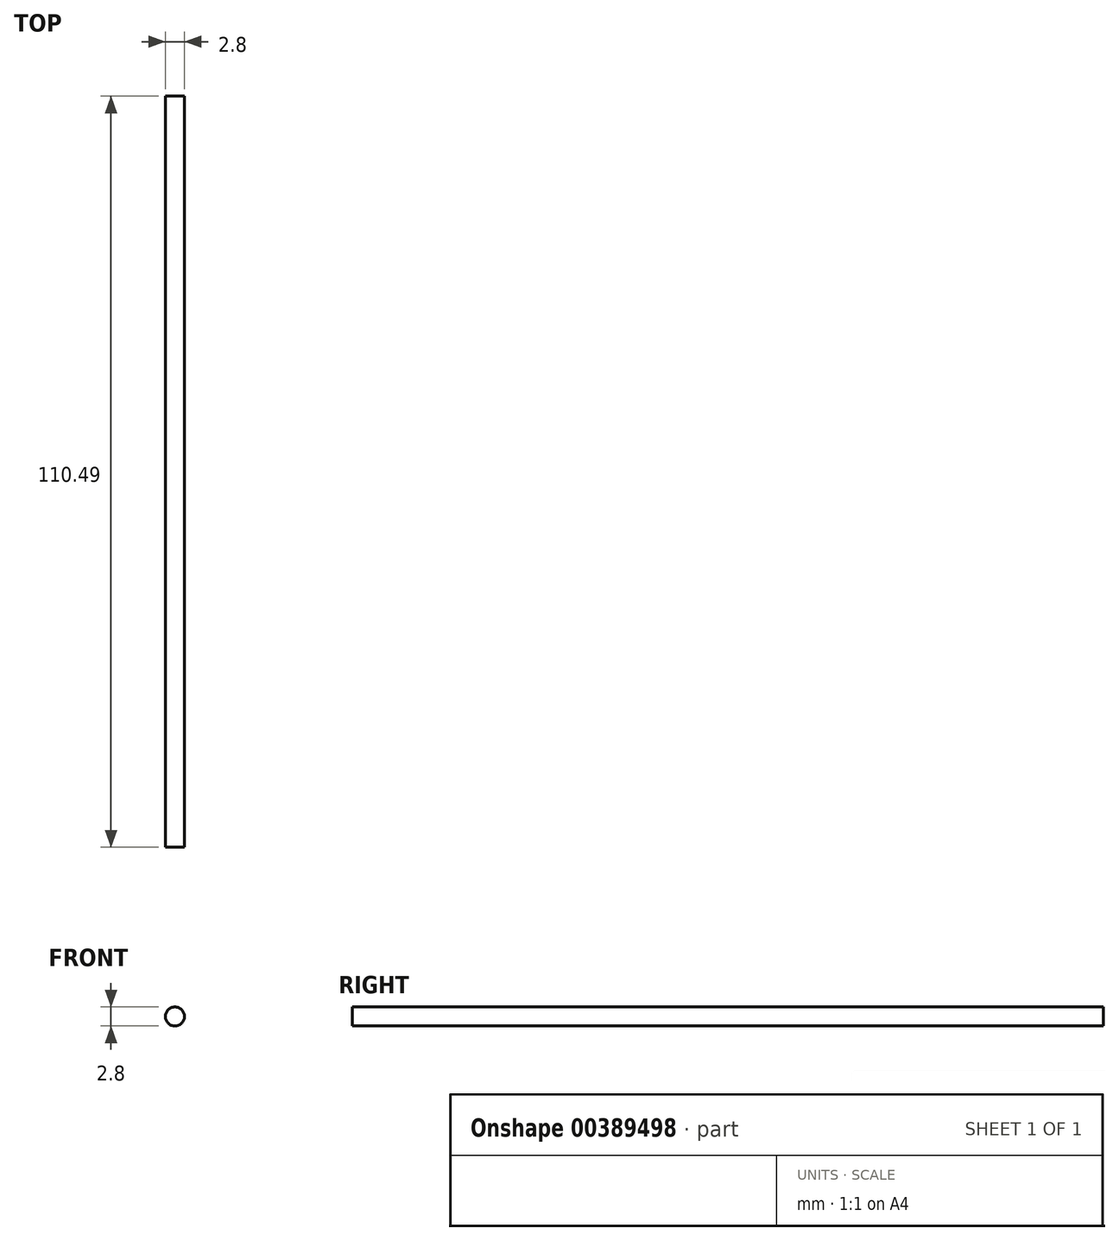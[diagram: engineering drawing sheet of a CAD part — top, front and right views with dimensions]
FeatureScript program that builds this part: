
annotation { "Feature Type Name" : "Feature", "Feature Type Description" : "" }
export const myFeature = defineFeature(function(context is Context, id is Id, definition is map)
    precondition{}
    {
        {
            var Q0;
            Q0=qCreatedBy(makeId("Front.planeOp"),FACE);
            var sketch = newSketch(context, id + "F0", { "sketchPlane" : qUnion([Q0])});
            skCircle(sketch, "E0", {"center": v(0, 0) * mm, "radius": 1.4 * mm});
            skSolve(sketch);
        }
        {
            var Q0;
            Q0 = qSketchRegion(id + "F0", true);
            extrude(context, id + "F1", {"entities" : qUnion([Q0]), "depth" : 110.49 * mm});
        }
    });
